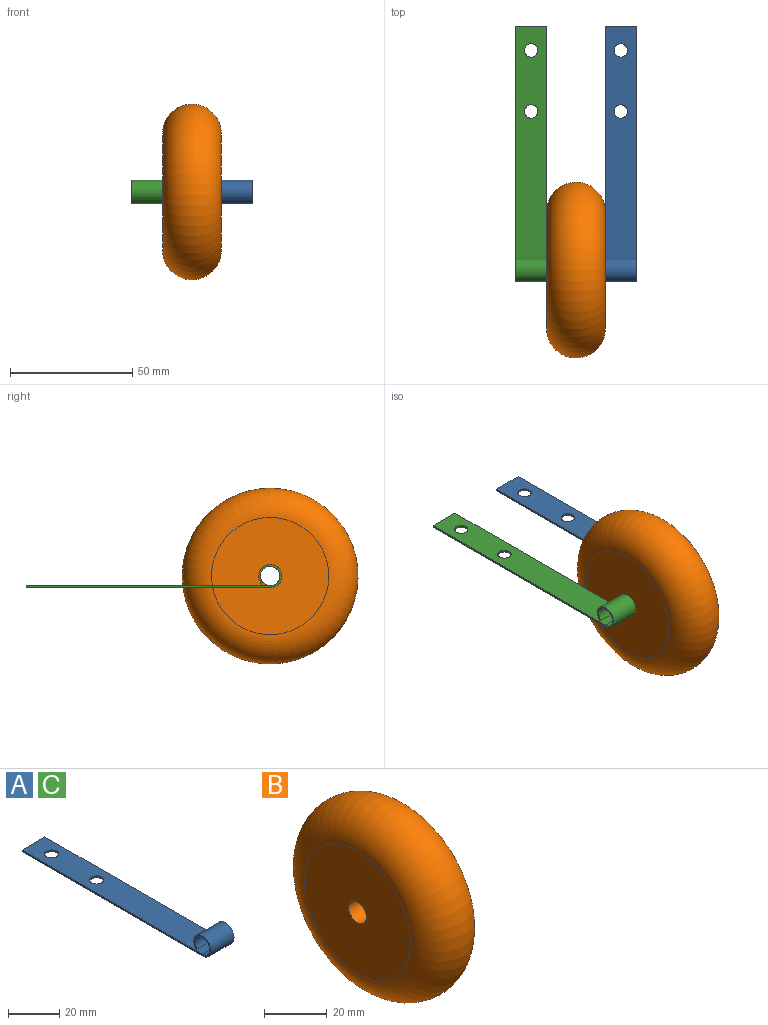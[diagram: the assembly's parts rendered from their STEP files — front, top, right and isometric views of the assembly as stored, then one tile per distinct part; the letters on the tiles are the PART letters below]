
ASSEMBLY  parts=3 mates=3
PART A: 10 faces, bbox 12.7x104.8x9.6 mm
  f0: cylinder r=4mm len=12.7mm, axis (-1,0,0), area 279.3mm2, adj f1,f5,f6,f7
  f1: plane 12.7x0.57mm, normal (0,-0.71,-0.71), area 10.2mm2, adj f0,f2,f6,f7
  f2: cylinder r=4.8mm len=12.7mm, axis (-1,0,0), area 335.1mm2, adj f1,f3,f6,f7
  f3: plane 100x12.7mm, normal (0,0,-1), area 1222.5mm2, adj f2,f4,f6,f7,f8,f9
  f4: plane 12.7x0.8mm, normal (0,1,0), area 10.2mm2, adj f3,f5,f6,f7
  f5: plane 100x12.7mm, normal (0,0,1), area 1222.5mm2, adj f0,f4,f6,f7,f8,f9
  f6: plane 104.8x9.6mm, normal (1,0,0), area 99.4mm2, adj f0,f1,f2,f3,f4,f5
  f7: plane 104.8x9.6mm, normal (-1,0,0), area 99.4mm2, adj f0,f1,f2,f3,f4,f5
  f8: cylinder r=2.75mm len=5.5mm, axis (0,0,-1), area 13.8mm2, adj f3,f5
  f9: cylinder r=2.75mm len=5.5mm, axis (0,0,-1), area 13.8mm2, adj f3,f5
PART B: 4 faces, bbox 24x77.9x77.9 mm
  f0: plane 48x48mm, normal (-1,0,0), area 1759.3mm2, adj f1,f3
  f1: cylinder r=4mm len=24mm, axis (-1,0,0), area 603.2mm2, adj f0,f2
  f2: plane 48x48mm, normal (1,0,0), area 1759.3mm2, adj f1,f3
  f3: torus R=24mm, axis (-1,0,0), area 7494.4mm2, adj f0,f2
PART C: same geometry as A
PLACE A t=(36.7,-90,0)mm
PLACE B t=(18.35,-90,4.8)mm
PLACE C t=(0,-90,0)mm
MATE planar C.f8 <-> A.f8  axis (0,0,1) through (0,-25,0.8)mm
MATE revolute C.f2 <-> B.f1  axis (-1,0,0) through (6.35,-90,4.8)mm
MATE revolute B.f1 <-> A.f0  axis (-1,0,0) through (30.35,-90,4.8)mm
